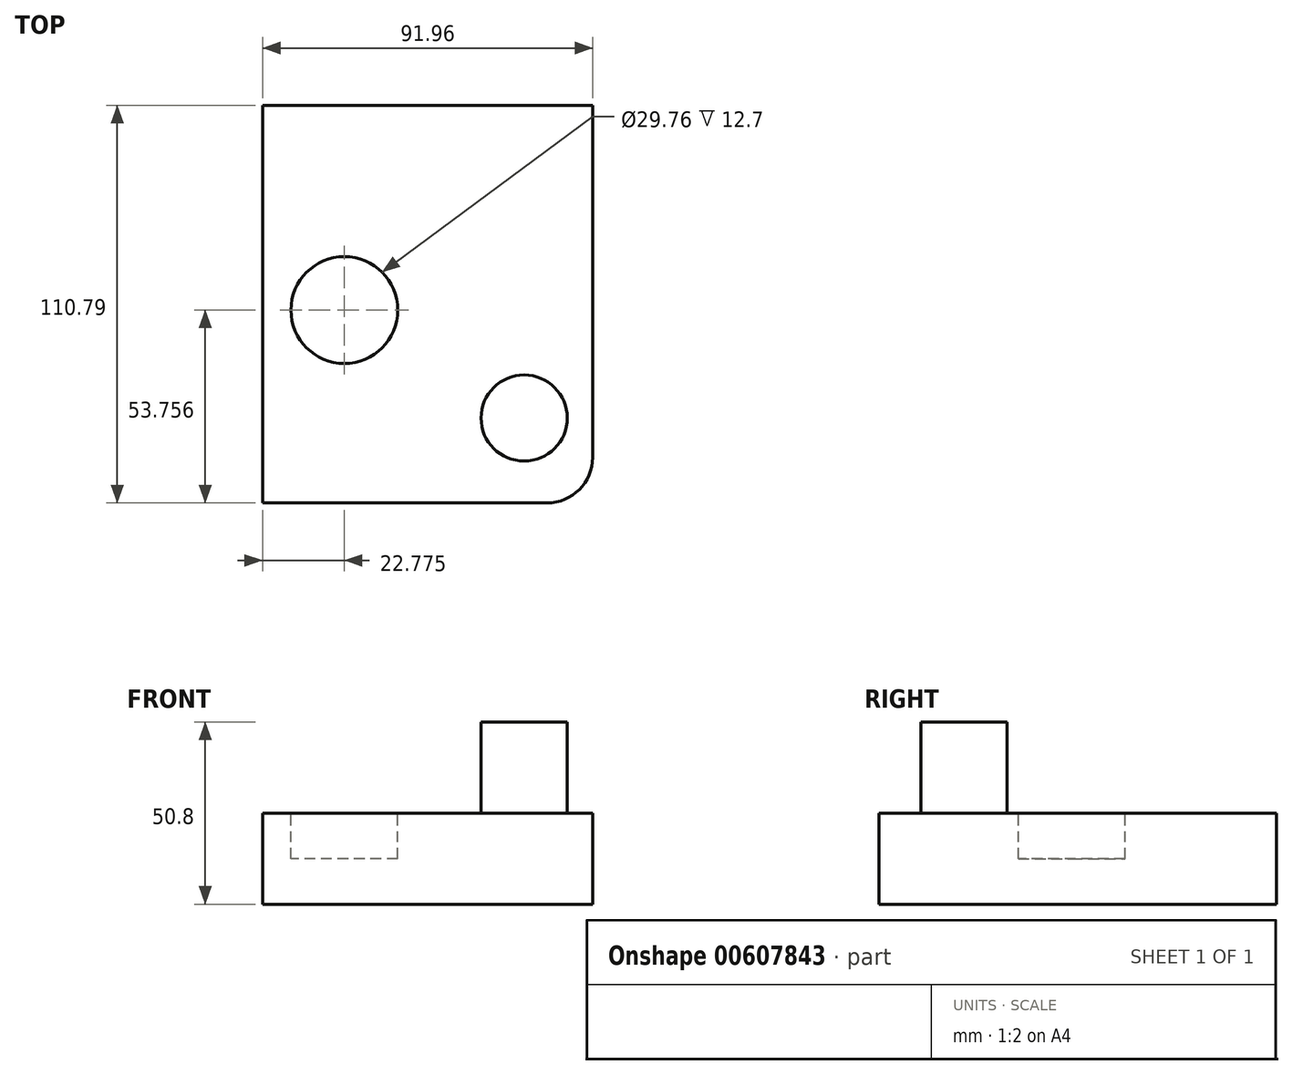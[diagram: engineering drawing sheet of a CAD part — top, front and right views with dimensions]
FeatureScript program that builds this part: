
annotation { "Feature Type Name" : "Feature", "Feature Type Description" : "" }
export const myFeature = defineFeature(function(context is Context, id is Id, definition is map)
    precondition{}
    {
        {
            var Q0;
            Q0=qCreatedBy(makeId("Top.planeOp"),FACE);
            var sketch = newSketch(context, id + "F0", { "sketchPlane" : qUnion([Q0])});
            skLineSegment(sketch, "E0.bottom", {"start": v(-46.05, -39.55) * mm, "end": v(45.9, -39.55) * mm});
            skLineSegment(sketch, "E0.top", {"start": v(-46.05, 71.24) * mm, "end": v(45.9, 71.24) * mm});
            skLineSegment(sketch, "E0.left", {"start": v(-46.05, -39.55) * mm, "end": v(-46.05, 71.24) * mm});
            skLineSegment(sketch, "E0.right", {"start": v(45.9, -39.55) * mm, "end": v(45.9, 71.24) * mm});
            skSolve(sketch);
        }
        {
            var Q0;
            Q0 = qSketchRegion(id + "F0", true);
            extrude(context, id + "F1", {"entities" : qUnion([Q0]), "depth" : 25.4 * mm, "offsetDistance" : 25.4 * mm});
        }
        {
            var Q0;
            Q0=makeQuery(id+"F1.opExtrude","SWEPT_EDGE",EDGE,{"disambiguationData":[OSD([sQuery(id+"F0.wireOp",EDGE,"E0.bottom"),sQuery(id+"F0.wireOp",EDGE,"E0.right")])]});
            fillet(context, id + "F2", {"entities" : qUnion([Q0]), "radius" : 12.7 * mm, "tangentPropagation" : true, "allowEdgeOverflow" : false});
        }
        {
            var Q0;
            Q0=makeQuery(id+"F1.opExtrude","CAP_FACE",FACE,{"disambiguationData":[OSD([sQuery(id+"F0.wireOp",EDGE,"E0.bottom"),sQuery(id+"F0.wireOp",EDGE,"E0.top"),sQuery(id+"F0.wireOp",EDGE,"E0.left"),sQuery(id+"F0.wireOp",EDGE,"E0.right")])],"isStart":false});
            var sketch = newSketch(context, id + "F3", { "sketchPlane" : qUnion([Q0])});
            skCircle(sketch, "E1", {"center": v(26.82, -15.86) * mm, "radius": 12 * mm});
            skSolve(sketch);
        }
        {
            var Q0;
            Q0 = qSketchRegion(id + "F3", true);
            extrude(context, id + "F4", {"entities" : qUnion([Q0]), "operationType" : NewBodyOperationType.ADD, "depth" : 25.4 * mm, "offsetDistance" : 25.4 * mm});
        }
        {
            var Q0;
            Q0=makeQuery(id+"F1.opExtrude","CAP_FACE",FACE,{"disambiguationData":[OSD([sQuery(id+"F0.wireOp",EDGE,"E0.bottom"),sQuery(id+"F0.wireOp",EDGE,"E0.top"),sQuery(id+"F0.wireOp",EDGE,"E0.left"),sQuery(id+"F0.wireOp",EDGE,"E0.right")])],"isStart":false});
            var sketch = newSketch(context, id + "F5", { "sketchPlane" : qUnion([Q0])});
            skCircle(sketch, "E2", {"center": v(-23.27, 14.2) * mm, "radius": 14.88 * mm});
            skSolve(sketch);
        }
        {
            var Q0;
            Q0 = qSketchRegion(id + "F5", true);
            extrude(context, id + "F6", {"entities" : qUnion([Q0]), "operationType" : NewBodyOperationType.REMOVE, "oppositeDirection" : true, "depth" : 12.7 * mm, "offsetDistance" : 25.4 * mm});
        }
    });
